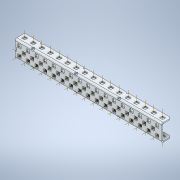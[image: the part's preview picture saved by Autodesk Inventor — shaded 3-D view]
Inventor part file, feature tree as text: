
AUTODESK INVENTOR PART (.ipt)
format: ipt  version: 2020 (Build 240168000, 168)  size: 1,348,608 bytes
history: native  units: in
note: dims shown in document units (in); Inventor stores cm internally (conversion verified against a paired STEP export)
features: other x88, plane x9, pattern_linear x4, split x4, sheet_metal_op x1
ambient origin geometry x8: Origin, YZ Plane, XZ Plane, XY Plane, X Axis, Y Axis, Z Axis, Center Point
bodies: Solid1 (feature_tree)
feature tree (106):
  other  "Work Axis1"
  pattern_linear  "Rectangular Pattern1"  Count1=17 Spacing1=0.5in
  other  "Work Axis72"
  pattern_linear  "Rectangular Pattern2"  Count1=17 Spacing1=0.5in
  pattern_linear  "Rectangular Pattern3"  Count1=17 Spacing1=0.5in
  other  "Work Axis141"
  pattern_linear  "Rectangular Pattern4"  Count1=16 Spacing1=0.5in
  plane  "Work Plane7"
  split  "Split1"
  plane  "Work Plane8"
  split  "Split2"
  split  "Split3"
  plane  "Work Plane9"
  split  "Split4"
  plane  "Work Plane1"
  plane  "Work Plane2"
  other  "Work Point1"
  other  "Work Axis2"
  other  "Work Axis3"
  other  "Work Axis4"
  other  "Work Axis5"
  other  "Work Axis6"
  other  "Work Axis7"
  other  "Work Axis8"
  other  "Work Axis9"
  other  "Work Axis10"
  other  "Work Axis11"
  other  "Work Axis12"
  other  "Work Axis13"
  other  "Work Axis14"
  other  "Work Axis15"
  other  "Work Axis16"
  other  "Work Axis17"
  other  "Work Axis36"
  other  "Work Axis37"
  other  "Work Axis38"
  other  "Work Axis39"
  other  "Work Axis40"
  other  "Work Axis41"
  other  "Work Axis42"
  other  "Work Axis43"
  other  "Work Axis44"
  other  "Work Axis45"
  other  "Work Axis46"
  other  "Work Axis47"
  other  "Work Axis48"
  other  "Work Axis49"
  other  "Work Axis50"
  other  "Work Axis51"
  other  "Work Axis52"
  plane  "Work Plane3"
  plane  "Work Plane4"
  other  "Work Point2"
  other  "Work Axis71"
  other  "Work Point3"
  other  "Work Axis73"
  other  "Work Axis74"
  other  "Work Axis75"
  other  "Work Axis76"
  other  "Work Axis77"
  other  "Work Axis78"
  other  "Work Axis79"
  other  "Work Axis80"
  other  "Work Axis81"
  other  "Work Axis82"
  other  "Work Axis83"
  other  "Work Axis84"
  other  "Work Axis85"
  other  "Work Axis86"
  other  "Work Axis87"
  other  "Work Axis88"
  other  "Work Axis107"
  other  "Work Axis108"
  other  "Work Axis109"
  other  "Work Axis110"
  other  "Work Axis111"
  other  "Work Axis112"
  other  "Work Axis113"
  other  "Work Axis114"
  other  "Work Axis115"
  other  "Work Axis116"
  other  "Work Axis117"
  other  "Work Axis118"
  other  "Work Axis119"
  other  "Work Axis120"
  other  "Work Axis121"
  other  "Work Axis122"
  plane  "Work Plane5"
  plane  "Work Plane6"
  other  "Work Point4"
  other  "Work Axis142"
  other  "Work Axis143"
  other  "Work Axis144"
  other  "Work Axis145"
  other  "Work Axis146"
  other  "Work Axis147"
  other  "Work Axis148"
  other  "Work Axis149"
  other  "Work Axis150"
  other  "Work Axis151"
  other  "Work Axis152"
  other  "Work Axis153"
  other  "Work Axis154"
  other  "Work Axis155"
  other  "Work Axis156"
  sheet_metal_op  "Fold1"
